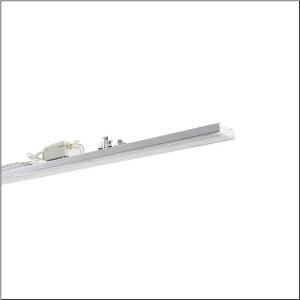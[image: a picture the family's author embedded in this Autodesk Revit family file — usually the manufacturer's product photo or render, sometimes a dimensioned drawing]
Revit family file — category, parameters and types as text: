
# Revit family: licross_21_recessed_ho_52te18dv4l2m
name_source: partatom
category: Lighting Fixtures
units: mm (PartAtom-declared; Revit-internal decimal feet)

## family parameters
Cut with Voids When Loaded = No
Host = Face
Light Source = No
Part Type = Normal
Room Calculation Point = No
Round Connector Dimension = Use Diameter
Shared = No

## types (1)
- --- (1 x LED, 22480 lm, 125.6 W, 4000K)
    Apparent Load = 126 VA
    CIE Flux Codes = 75 94 99 100 100
    Color Rendering = 80
    Color Temperature = 4000K
    Default Elevation = 1800 mm
    Description = Licross 21 Recessed HO, luminaire insert, of sheet steel, galvanised, coil coated, white, length: 2.250mm, width: 66mm, height: 67mm, LED rated luminous flux: 22.480lm, light colour: 840, SDCM (Standard Deviation of Colour Matching)MacAdam ≤ 3 SDCM (initial), control gear: DALI 2, with plug, 5-pole, with phase selection, mains connection: 220..240V, AC, 50/60Hz, rated input power: 126W, internal wiring halogen-free, primary light control with lens, of plastic, primary optical cover: cover, of PMMA, light emission: direct distribution, primary light characteristic: symmetric, protection rating (complete): IP54, insulation class (complete): insulation class I (protective earthing), certification: CE, ENEC, VDE, UKCA, protection symbol: D if used in an environment with non-conductive dust loads with corresponding accessories, impact resistance: IK06, permissible ambient temperature for indoor applications: -40..+30°C, corresponds to IFS (International Featured Standards) requirements for safety and quality in the food industry, reducing of maximum allowable ambient temperature of 5°C with ceiling mounting, LABS conformity tested according to VDMA 24364:2018-05, The light source and the operating device comply with the requirements of the Ecodesign Regulation (EU) 2019/2020 and are replaceable in accordance with this regulation, packaging unit: 1 piece
    Height = 58 mm
    Lamp = 1 x LED
    Lamp Light Flux = 22480 lm
    Lamp Power = 125.6 W
    Lamp count = 1
    Length = 2250 mm
    Luminous efficacy = 179 lm/W
    Manufacturer = Siteco
    ModVariant = No
    Model = 52TE18DV4L2M
    Mounting Place = Ceiling
    Mounting Type = Pendant
    Number of Poles = 1
    OnlyDefault = Yes
    Power Factor = 1
    Product Name = Licross 21 Recessed HO
    Product group = luminaire insert | ceiling pendant
    ProductGroupID = 901
    Protection Class = Protection class I
    Protection Degree = IP 54
    RLX_Detail_Level = 1
    RLX_Emergency_Light_Flux = 0 lm
    RLX_Emergency_Type = 0
    RLX_Emergency_Type_DB = No
    RlxData = <blob elided: 30021 chars, md5=d9f24e13>
    Socket = socket
    Standby Power = 0 W
    System Light Flux = 22480 lm
    System Power = 126 W
    Type Comments = factory setting: luminous flux: 100 % | dim-lin: 254 | 489 mA
    Type Image = l_1296930.jpg
    URL = http://relux.com
    VarID = @adj_127517
    Voltage = 0 V
    Weight = 0.00 kg
    Width = 66 mm

## geometry (parser evidence)
native form markers: Blend x4, Sweep x10
no freeform markers — native parametric forms only
